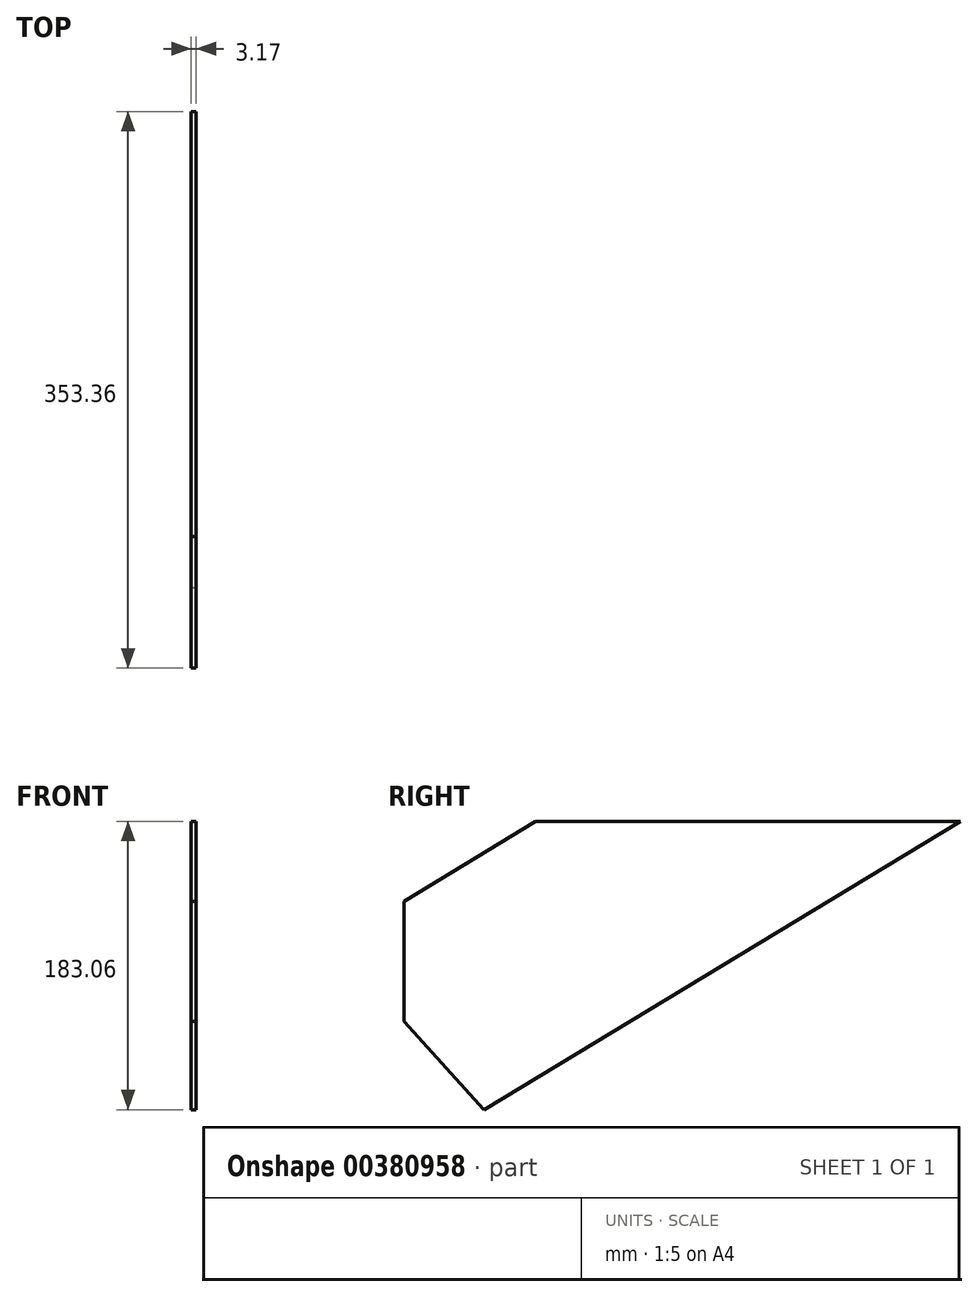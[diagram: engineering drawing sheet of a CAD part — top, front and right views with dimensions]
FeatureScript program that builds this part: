
annotation { "Feature Type Name" : "Feature", "Feature Type Description" : "" }
export const myFeature = defineFeature(function(context is Context, id is Id, definition is map)
    precondition{}
    {
        {
            var Q0;
            Q0=qCreatedBy(makeId("Right.planeOp"),FACE);
            var sketch = newSketch(context, id + "F0", { "sketchPlane" : qUnion([Q0])});
            skLineSegment(sketch, "E0.bottom", {"start": v(-93.2, 88.9) * mm, "end": v(176.68, 88.9) * mm});
            skLineSegment(sketch, "E0.left", {"start": v(-176.68, 38.1) * mm, "end": v(-176.68, -38.1) * mm});
            skPoint(sketch, "E0.middle", {"position": v(0, 0) * mm});
            skLineSegment(sketch, "E1", {"start": v(176.68, 88.9) * mm, "end": v(-125.88, -94.16) * mm});
            skLineSegment(sketch, "E2", {"start": v(-93.2, 88.9) * mm, "end": v(-176.68, 38.1) * mm});
            skLineSegment(sketch, "E3", {"start": v(-176.68, -38.1) * mm, "end": v(-125.88, -94.16) * mm});
            skPoint(sketch, "E4.orphan", {"position": v(176.68, -88.9) * mm});
            skPoint(sketch, "E0.top.start.orphan", {"position": v(-176.68, -88.9) * mm});
            skPoint(sketch, "E5.orphan", {"position": v(-176.68, 88.9) * mm});
            skSolve(sketch);
        }
        {
            var Q0;
            Q0=qSketchRegion(id+"F0",true);
            extrude(context, id + "F1", {"entities" : qUnion([Q0]), "depth" : 3.17 * mm});
        }
    });
